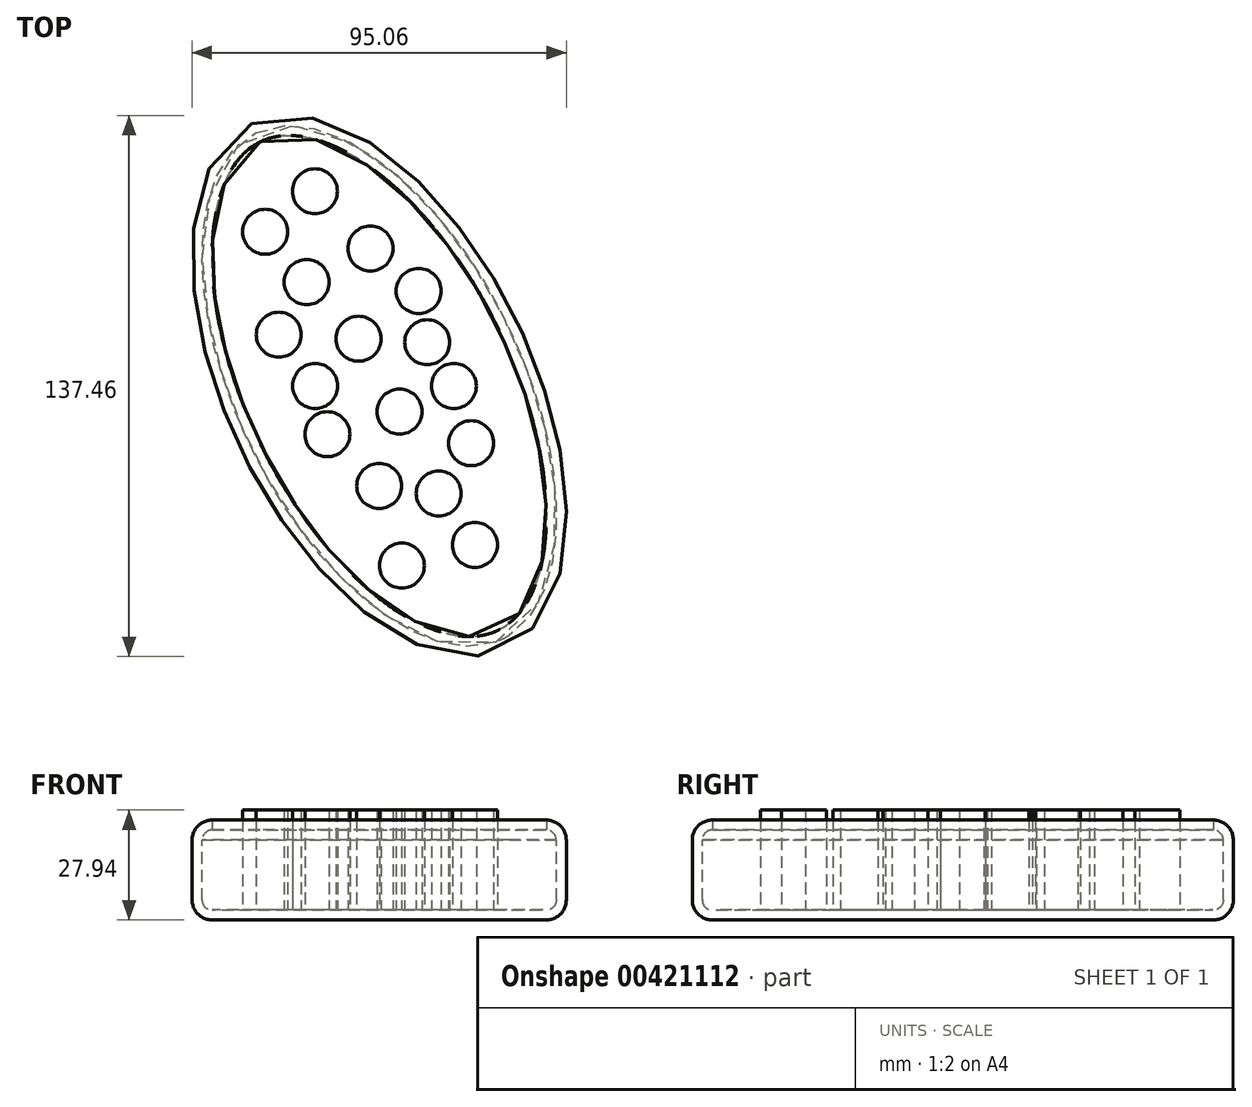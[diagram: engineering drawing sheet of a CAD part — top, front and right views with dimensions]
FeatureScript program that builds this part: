
annotation { "Feature Type Name" : "Feature", "Feature Type Description" : "" }
export const myFeature = defineFeature(function(context is Context, id is Id, definition is map)
    precondition{}
    {
        {
            var Q0;
            Q0=qCreatedBy(makeId("Top.planeOp"),FACE);
            var sketch = newSketch(context, id + "F0", { "sketchPlane" : qUnion([Q0])});
            skEllipse(sketch, "E0", {"center": v(0, 0) * mm, "majorRadius": 38.65 * mm, "minorRadius": 74.09 * mm, "majorAxis": v(0.9, 0.44)});
            skSolve(sketch);
        }
        {
            var Q0;
            Q0 = qSketchRegion(id + "F0", true);
            extrude(context, id + "F1", {"entities" : qUnion([Q0]), "depth" : 25.4 * mm});
        }
        {
            var Q0;
            Q0=makeQuery(id+"F1.opExtrude","CAP_EDGE",EDGE,{"disambiguationData":[OSD([sQuery(id+"F0.wireOp",EDGE,"E0")])],"isStart":false});
            var Q1;
            Q1=makeQuery(id+"F1.opExtrude","SWEPT_FACE",FACE,{"disambiguationData":[OSD([sQuery(id+"F0.wireOp",EDGE,"E0")])]});
            var Q2;
            Q2=makeQuery(id+"F1.opExtrude","CAP_EDGE",EDGE,{"disambiguationData":[OSD([sQuery(id+"F0.wireOp",EDGE,"E0")])],"isStart":true});
            var Q3;
            Q3=makeQuery(id+"F1.opExtrude","CAP_FACE",FACE,{"disambiguationData":[OSD([sQuery(id+"F0.wireOp",EDGE,"E0")])],"isStart":false});
            fillet(context, id + "F2", {"entities" : qUnion([Q0, Q1, Q2, Q3]), "radius" : 5.08 * mm, "tangentPropagation" : true, "allowEdgeOverflow" : false});
        }
        {
            var Q0;
            Q0=makeQuery(id+"F1.opExtrude","CAP_FACE",FACE,{"disambiguationData":[OSD([sQuery(id+"F0.wireOp",EDGE,"E0")])],"isStart":false});
            shell(context, id + "F3", {"entities" : qUnion([Q0]), "thickness" : 2.54 * mm});
        }
        {
            var Q0;
            {var subQ0=sQuery(id+"F0.wireOp",EDGE,"E0");Q0=makeQuery(id+"F3.opShell","OFFSET_FACE",FACE,{"disambiguationData":[OSD([subQ0]),TDD([makeQuery(id+"F1.opExtrude","CAP_FACE",FACE,{"disambiguationData":[OSD([subQ0])],"isStart":true})])]});}
            var sketch = newSketch(context, id + "F4", { "sketchPlane" : qUnion([Q0])});
            skCircle(sketch, "E1", {"center": v(-28.97, 39.18) * mm, "radius": 5.72 * mm});
            skSolve(sketch);
        }
        {
            var Q0;
            Q0 = qSketchRegion(id + "F4", true);
            extrude(context, id + "F5", {"entities" : qUnion([Q0]), "operationType" : NewBodyOperationType.ADD, "depth" : 25.4 * mm});
        }
        {
            var Q0;
            {var subQ0=sQuery(id+"F0.wireOp",EDGE,"E0");Q0=makeQuery(id+"F3.opShell","OFFSET_FACE",FACE,{"disambiguationData":[OSD([subQ0]),TDD([makeQuery(id+"F1.opExtrude","CAP_FACE",FACE,{"disambiguationData":[OSD([subQ0])],"isStart":true})])]});}
            var sketch = newSketch(context, id + "F6", { "sketchPlane" : qUnion([Q0])});
            skCircle(sketch, "E2", {"center": v(-25.52, 13.04) * mm, "radius": 5.72 * mm});
            skSolve(sketch);
        }
        {
            var Q0;
            Q0 = qSketchRegion(id + "F6", true);
            extrude(context, id + "F7", {"entities" : qUnion([Q0]), "operationType" : NewBodyOperationType.ADD, "depth" : 25.4 * mm});
        }
        {
            var Q0;
            {var subQ0=sQuery(id+"F0.wireOp",EDGE,"E0");Q0=makeQuery(id+"F3.opShell","OFFSET_FACE",FACE,{"disambiguationData":[OSD([subQ0]),TDD([makeQuery(id+"F1.opExtrude","CAP_FACE",FACE,{"disambiguationData":[OSD([subQ0])],"isStart":true})])]});}
            var sketch = newSketch(context, id + "F8", { "sketchPlane" : qUnion([Q0])});
            skCircle(sketch, "E3", {"center": v(-13.17, -12.25) * mm, "radius": 5.72 * mm});
            skSolve(sketch);
        }
        {
            var Q0;
            Q0 = qSketchRegion(id + "F8", true);
            extrude(context, id + "F9", {"entities" : qUnion([Q0]), "operationType" : NewBodyOperationType.ADD, "depth" : 25.4 * mm});
        }
        {
            var Q0;
            {var subQ0=sQuery(id+"F0.wireOp",EDGE,"E0");Q0=makeQuery(id+"F3.opShell","OFFSET_FACE",FACE,{"disambiguationData":[OSD([subQ0]),TDD([makeQuery(id+"F1.opExtrude","CAP_FACE",FACE,{"disambiguationData":[OSD([subQ0])],"isStart":true})])]});}
            var sketch = newSketch(context, id + "F10", { "sketchPlane" : qUnion([Q0])});
            skCircle(sketch, "E4", {"center": v(0, -25.4) * mm, "radius": 5.72 * mm});
            skSolve(sketch);
        }
        {
            var Q0;
            Q0 = qSketchRegion(id + "F10", true);
            extrude(context, id + "F11", {"entities" : qUnion([Q0]), "operationType" : NewBodyOperationType.ADD, "depth" : 25.4 * mm});
        }
        {
            var Q0;
            {var subQ0=sQuery(id+"F0.wireOp",EDGE,"E0");Q0=makeQuery(id+"F3.opShell","OFFSET_FACE",FACE,{"disambiguationData":[OSD([subQ0]),TDD([makeQuery(id+"F1.opExtrude","CAP_FACE",FACE,{"disambiguationData":[OSD([subQ0])],"isStart":true})])]});}
            var sketch = newSketch(context, id + "F12", { "sketchPlane" : qUnion([Q0])});
            skCircle(sketch, "E5", {"center": v(24.32, -40.37) * mm, "radius": 5.72 * mm});
            skSolve(sketch);
        }
        {
            var Q0;
            Q0 = qSketchRegion(id + "F12", true);
            extrude(context, id + "F13", {"entities" : qUnion([Q0]), "operationType" : NewBodyOperationType.ADD, "depth" : 25.4 * mm});
        }
        {
            var Q0;
            {var subQ0=sQuery(id+"F0.wireOp",EDGE,"E0");Q0=makeQuery(id+"F3.opShell","OFFSET_FACE",FACE,{"disambiguationData":[OSD([subQ0]),TDD([makeQuery(id+"F1.opExtrude","CAP_FACE",FACE,{"disambiguationData":[OSD([subQ0])],"isStart":true})])]});}
            var sketch = newSketch(context, id + "F14", { "sketchPlane" : qUnion([Q0])});
            skCircle(sketch, "E6", {"center": v(12.2, 11.13) * mm, "radius": 5.72 * mm});
            skSolve(sketch);
        }
        {
            var Q0;
            Q0 = qSketchRegion(id + "F14", true);
            extrude(context, id + "F15", {"entities" : qUnion([Q0]), "operationType" : NewBodyOperationType.ADD, "depth" : 25.4 * mm});
        }
        {
            var Q0;
            {var subQ0=sQuery(id+"F0.wireOp",EDGE,"E0");Q0=makeQuery(id+"F3.opShell","OFFSET_FACE",FACE,{"disambiguationData":[OSD([subQ0]),TDD([makeQuery(id+"F1.opExtrude","CAP_FACE",FACE,{"disambiguationData":[OSD([subQ0])],"isStart":true})])]});}
            var sketch = newSketch(context, id + "F16", { "sketchPlane" : qUnion([Q0])});
            skCircle(sketch, "E7", {"center": v(-2.23, 34.94) * mm, "radius": 5.72 * mm});
            skSolve(sketch);
        }
        {
            var Q0;
            Q0 = qSketchRegion(id + "F16", true);
            extrude(context, id + "F17", {"entities" : qUnion([Q0]), "operationType" : NewBodyOperationType.ADD, "depth" : 25.4 * mm});
        }
        {
            var Q0;
            {var subQ0=sQuery(id+"F0.wireOp",EDGE,"E0");Q0=makeQuery(id+"F3.opShell","OFFSET_FACE",FACE,{"disambiguationData":[OSD([subQ0]),TDD([makeQuery(id+"F1.opExtrude","CAP_FACE",FACE,{"disambiguationData":[OSD([subQ0])],"isStart":true})])]});}
            var sketch = newSketch(context, id + "F18", { "sketchPlane" : qUnion([Q0])});
            skCircle(sketch, "E8", {"center": v(23.36, -14.54) * mm, "radius": 5.72 * mm});
            skSolve(sketch);
        }
        {
            var Q0;
            Q0 = qSketchRegion(id + "F18", true);
            extrude(context, id + "F19", {"entities" : qUnion([Q0]), "operationType" : NewBodyOperationType.ADD, "depth" : 25.4 * mm});
        }
        {
            var Q0;
            {var subQ0=sQuery(id+"F0.wireOp",EDGE,"E0");Q0=makeQuery(id+"F3.opShell","OFFSET_FACE",FACE,{"disambiguationData":[OSD([subQ0]),TDD([makeQuery(id+"F1.opExtrude","CAP_FACE",FACE,{"disambiguationData":[OSD([subQ0])],"isStart":true})])]});}
            var sketch = newSketch(context, id + "F20", { "sketchPlane" : qUnion([Q0])});
            skCircle(sketch, "E9", {"center": v(-5.25, 12) * mm, "radius": 5.72 * mm});
            skSolve(sketch);
        }
        {
            var Q0;
            Q0 = qSketchRegion(id + "F20", true);
            extrude(context, id + "F21", {"entities" : qUnion([Q0]), "operationType" : NewBodyOperationType.ADD, "depth" : 25.4 * mm});
        }
        {
            var Q0;
            {var subQ0=sQuery(id+"F0.wireOp",EDGE,"E0");Q0=makeQuery(id+"F3.opShell","OFFSET_FACE",FACE,{"disambiguationData":[OSD([subQ0]),TDD([makeQuery(id+"F1.opExtrude","CAP_FACE",FACE,{"disambiguationData":[OSD([subQ0])],"isStart":true})])]});}
            var sketch = newSketch(context, id + "F22", { "sketchPlane" : qUnion([Q0])});
            skCircle(sketch, "E10", {"center": v(5.17, -6.5) * mm, "radius": 5.72 * mm});
            skSolve(sketch);
        }
        {
            var Q0;
            Q0 = qSketchRegion(id + "F22", true);
            extrude(context, id + "F23", {"entities" : qUnion([Q0]), "operationType" : NewBodyOperationType.ADD, "depth" : 25.4 * mm});
        }
        {
            var Q0;
            {var subQ0=sQuery(id+"F0.wireOp",EDGE,"E0");Q0=makeQuery(id+"F3.opShell","OFFSET_FACE",FACE,{"disambiguationData":[OSD([subQ0]),TDD([makeQuery(id+"F1.opExtrude","CAP_FACE",FACE,{"disambiguationData":[OSD([subQ0])],"isStart":true})])]});}
            var sketch = newSketch(context, id + "F24", { "sketchPlane" : qUnion([Q0])});
            skCircle(sketch, "E11", {"center": v(5.76, -45.63) * mm, "radius": 5.72 * mm});
            skSolve(sketch);
        }
        {
            var Q0;
            Q0 = qSketchRegion(id + "F24", true);
            extrude(context, id + "F25", {"entities" : qUnion([Q0]), "operationType" : NewBodyOperationType.ADD, "depth" : 25.4 * mm});
        }
        {
            var Q0;
            {var subQ0=sQuery(id+"F0.wireOp",EDGE,"E0");Q0=makeQuery(id+"F3.opShell","OFFSET_FACE",FACE,{"disambiguationData":[OSD([subQ0]),TDD([makeQuery(id+"F1.opExtrude","CAP_FACE",FACE,{"disambiguationData":[OSD([subQ0])],"isStart":true})])]});}
            var sketch = newSketch(context, id + "F26", { "sketchPlane" : qUnion([Q0])});
            skCircle(sketch, "E12", {"center": v(-18.43, 26.4) * mm, "radius": 5.72 * mm});
            skSolve(sketch);
        }
        {
            var Q0;
            Q0 = qSketchRegion(id + "F26", true);
            extrude(context, id + "F27", {"entities" : qUnion([Q0]), "operationType" : NewBodyOperationType.ADD, "depth" : 25.4 * mm});
        }
        {
            var Q0;
            {var subQ0=sQuery(id+"F0.wireOp",EDGE,"E0");Q0=makeQuery(id+"F3.opShell","OFFSET_FACE",FACE,{"disambiguationData":[OSD([subQ0]),TDD([makeQuery(id+"F1.opExtrude","CAP_FACE",FACE,{"disambiguationData":[OSD([subQ0])],"isStart":true})])]});}
            var sketch = newSketch(context, id + "F28", { "sketchPlane" : qUnion([Q0])});
            skCircle(sketch, "E13", {"center": v(15.13, -27.31) * mm, "radius": 5.72 * mm});
            skSolve(sketch);
        }
        {
            var Q0;
            Q0 = qSketchRegion(id + "F28", true);
            extrude(context, id + "F29", {"entities" : qUnion([Q0]), "operationType" : NewBodyOperationType.ADD, "depth" : 25.4 * mm});
        }
        {
            var Q0;
            {var subQ0=sQuery(id+"F0.wireOp",EDGE,"E0");Q0=makeQuery(id+"F3.opShell","OFFSET_FACE",FACE,{"disambiguationData":[OSD([subQ0]),TDD([makeQuery(id+"F1.opExtrude","CAP_FACE",FACE,{"disambiguationData":[OSD([subQ0])],"isStart":true})])]});}
            var sketch = newSketch(context, id + "F30", { "sketchPlane" : qUnion([Q0])});
            skCircle(sketch, "E14", {"center": v(10.02, 24.14) * mm, "radius": 5.72 * mm});
            skSolve(sketch);
        }
        {
            var Q0;
            Q0 = qSketchRegion(id + "F30", true);
            extrude(context, id + "F31", {"entities" : qUnion([Q0]), "operationType" : NewBodyOperationType.ADD, "depth" : 25.4 * mm});
        }
        {
            var Q0;
            {var subQ0=sQuery(id+"F0.wireOp",EDGE,"E0");Q0=makeQuery(id+"F3.opShell","OFFSET_FACE",FACE,{"disambiguationData":[OSD([subQ0]),TDD([makeQuery(id+"F1.opExtrude","CAP_FACE",FACE,{"disambiguationData":[OSD([subQ0])],"isStart":true})])]});}
            var sketch = newSketch(context, id + "F32", { "sketchPlane" : qUnion([Q0])});
            skCircle(sketch, "E15", {"center": v(-16.28, 0) * mm, "radius": 5.72 * mm});
            skSolve(sketch);
        }
        {
            var Q0;
            Q0 = qSketchRegion(id + "F32", true);
            extrude(context, id + "F33", {"entities" : qUnion([Q0]), "operationType" : NewBodyOperationType.ADD, "depth" : 25.4 * mm});
        }
        {
            var Q0;
            {var subQ0=sQuery(id+"F0.wireOp",EDGE,"E0");Q0=makeQuery(id+"F3.opShell","OFFSET_FACE",FACE,{"disambiguationData":[OSD([subQ0]),TDD([makeQuery(id+"F1.opExtrude","CAP_FACE",FACE,{"disambiguationData":[OSD([subQ0])],"isStart":true})])]});}
            var sketch = newSketch(context, id + "F34", { "sketchPlane" : qUnion([Q0])});
            skCircle(sketch, "E16", {"center": v(-16.32, 49.48) * mm, "radius": 5.72 * mm});
            skSolve(sketch);
        }
        {
            var Q0;
            Q0 = qSketchRegion(id + "F34", true);
            extrude(context, id + "F35", {"entities" : qUnion([Q0]), "operationType" : NewBodyOperationType.ADD, "depth" : 25.4 * mm});
        }
        {
            var Q0;
            {var subQ0=sQuery(id+"F0.wireOp",EDGE,"E0");Q0=makeQuery(id+"F3.opShell","OFFSET_FACE",FACE,{"disambiguationData":[OSD([subQ0]),TDD([makeQuery(id+"F1.opExtrude","CAP_FACE",FACE,{"disambiguationData":[OSD([subQ0])],"isStart":true})])]});}
            var sketch = newSketch(context, id + "F36", { "sketchPlane" : qUnion([Q0])});
            skCircle(sketch, "E17", {"center": v(18.97, 0) * mm, "radius": 5.72 * mm});
            skSolve(sketch);
        }
        {
            var Q0;
            Q0 = qSketchRegion(id + "F36", true);
            extrude(context, id + "F37", {"entities" : qUnion([Q0]), "operationType" : NewBodyOperationType.ADD, "depth" : 25.4 * mm});
        }
    });
